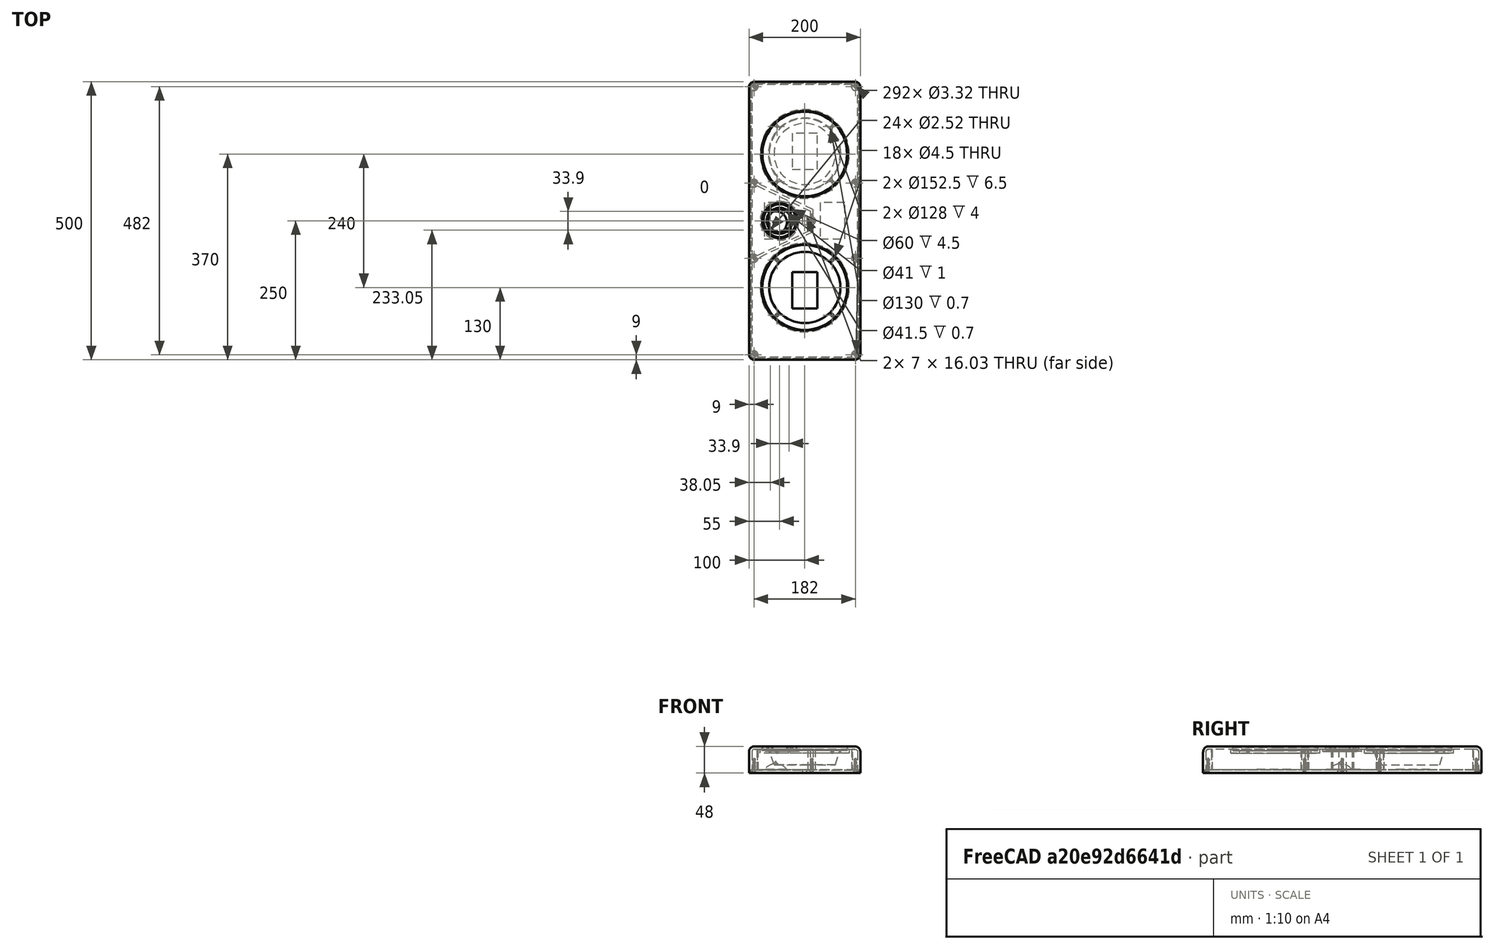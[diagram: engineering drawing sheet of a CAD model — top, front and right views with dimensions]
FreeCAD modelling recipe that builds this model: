
FCSTD DOCUMENT  (FreeCAD 1.1R14555 (Git shallow))
Label: wallspeakers prototype v4
License: All rights reserved
LicenseURL: http://en.wikipedia.org/wiki/All_rights_reserved
objects: Sketcher::SketchObject×23, PartDesign::Pad×11, App::Point×9, PartDesign::Body×9, PartDesign::Pocket×7, TechDraw::DrawViewAnnotation×6, TechDraw::DrawViewImage×6, PartDesign::Hole×5, TechDraw::DrawSVGTemplate×5, TechDraw::DrawPage×5, App::DocumentObjectGroup×4, TechDraw::DrawViewDimExtent×3, PartDesign::Chamfer×3, PartDesign::Revolution×2, PartDesign::Fillet×2, TechDraw::DrawProjGroupItem×2, Spreadsheet::Sheet×1, PartDesign::Thickness×1, TechDraw::DrawProjGroup×1, PartDesign::SubShapeBinder×1, +3 more types
note: 152 computed .brp shape members not serialized (recipe doc carries the construction recipe); baked Part::Feature solids carry a one-line shape summary decoded from their .brp

FEATURE [Spreadsheet::Sheet] Spreadsheet  label="dim"
  cells = A1='ext_width; B1(ext_width)=200; A2='ext_length; B2(ext_length)=500; A3='back_panel_width; B3(back_panel_width)==B1 - B13 * 2; C3='ext_width - rim_width * 2; A4='back_panel_length; B4(back_panel_length)==B2 - B13 * 2; C4='ext_length - rim_width * 2; A5='back_panel_radius; B5(back_panel_radius)==B11 - B13; C5='corner_roundover - rim_width; A6='back_thickness; B6(back_thickness)=5; A7='front_thickness; B7(front_thickness)=5; A8='total_depth; B8(total_depth)=48; C8='giving ourselves 2mm for wall mount fittings etc; A9='wall_thickness; B9(wall_thickness)=5; A10='front_roundover; B10(front_roundover)=10; A11='corner_roundover; B11(corner_roundover)=10; A13='rim_width; B13(rim_width)=3; A14='rim_depth; B14(rim_depth)=5.7; C14='allowing 0.7mm for a compressed 0.8mm gasket; A15='post_diameter; B15(post_diameter)=14; A17='bmr_x; B17(bmr_x)=45; C17='nudging a bit closer to the centre; A18='bmr_y; B18(bmr_y)=0; A19='bmr_screw_distance; B19(bmr_screw_distance)=24; A20='bmr_screw_offset; B20(bmr_screw_offset)=16.95; C20='bmr_screw_distance * sin(45); A21='bmr_hole_diameter; B21(bmr_hole_diameter)=41; A22='bmr_rebate_depth; B22(bmr_rebate_depth)=6; A23='bmr_post_width; B23(bmr_post_width)=7; A24='bmr_rebate_diameter; B24(bmr_rebate_diameter)=60; A26='woofer_x; B26(woofer_x)=0; A27='woofer_y; B27(woofer_y)=120; A28='woofer_support_thickness; B28(woofer_support_thickness)=7; C28='resulting in wall (5mm) + this (7mm) - rebate (8mm) = 5mm; A29='woofer_support_diameter; B29(woofer_support_diameter)=160; A30='woofer_screw_distance; B30(woofer_screw_thickness)=70.05; A31='woofer_screw_offset; B31(woofer_screw_offset)==B30 * 0.707; C31='woofer_screw_distance * sin(45); A32='woofer_hole_diameter; B32(woofer_hole_diameter)=128; A33='woofer_rebate_depth; B33(woofer_rebate_depth)=8; C33='5.3 for woofer rim, 0.7 for compressed gasket, 2 for cone resting excursion; A34='woofer_rebate_diameter; B34(woofer_rebate_diameter)=152.5; A39='woofer cutout spec; B39=127.5; C39=0.3; A40='woofer rebate spec; B40=152; C40=0.3; A41='woofer rebate depth spec; B41=5.3; C41=0.3; A43='gasket thickness (compressed); B43=0.7
FEATURE [Sketcher::SketchObject] Sketch  label="outline"
  ArcFitTolerance = 1e-06
  AttachmentSupport = -> [XY_Plane]
  ExternalTypes = [0]
  FullyConstrained = true
  MakeInternals = false
  MapMode = 5
  expr: Constraints[8] = <<dim>>.ext_width
  expr: Constraints[9] = <<dim>>.ext_length
  sketch-geometry (4):
    g0: LineSegment StartX=-100 StartY=250 StartZ=0 EndX=-100 EndY=-250 EndZ=0
    g1: LineSegment StartX=-100 StartY=-250 StartZ=0 EndX=100 EndY=-250 EndZ=0
    g2: LineSegment StartX=100 StartY=-250 StartZ=0 EndX=100 EndY=250 EndZ=0
    g3: LineSegment StartX=100 StartY=250 StartZ=0 EndX=-100 EndY=250 EndZ=0
  constraints (10):
    c: Coincident(g0,g1)
    c: Coincident(g1,g2)
    c: Coincident(g2,g3)
    c: Coincident(g3,g0)
    c: Vertical(g0)
    c: Horizontal(g1)
    c: Symmetric(g0,g2,g-2)
    c: Symmetric(g2,g1,g-1)
    c: DistanceX(g3,g3) = 200
    c: DistanceY(g2,g2) = 500
FEATURE [PartDesign::Pad] Pad  label="main solid body"
  Direction = (0,0,1)
  Length = 48
  Length2 = 10
  Profile = -> Sketch
  ReferenceAxis = -> Sketch [N_Axis]
  SideType = 0
  Suppressed = false
  Type = 0
  Type2 = 0
  expr: Length = <<dim>>.total_depth
FEATURE [Sketcher::SketchObject] Sketch002  label="woofer rebates"
  ArcFitTolerance = 1e-06
  AttachmentSupport = -> [Pad]
  ExternalTypes = [0]
  FullyConstrained = true
  MakeInternals = false
  MapMode = 5
  Placement = pos=(0,0,48) rot=(0,0,1;0rad)
  expr: Constraints[0] = <<dim>>.woofer_x
  expr: Constraints[1] = <<dim>>.woofer_y
  expr: Constraints[2] = <<dim>>.woofer_rebate_diameter
  expr: Constraints[3] = <<dim>>.woofer_rebate_diameter
  expr: Constraints[4] = <<dim>>.woofer_x
  expr: Constraints[5] = <<dim>>.woofer_y
  sketch-geometry (2):
    g0: Circle CenterX=0 CenterY=120 CenterZ=0 NormalX=0 NormalY=0 NormalZ=1 AngleXU=0 Radius=76.25
    g1: Circle CenterX=0 CenterY=-120 CenterZ=0 NormalX=0 NormalY=0 NormalZ=1 AngleXU=0 Radius=76.25
  constraints (6):
    c: DistanceX(g0,g-1) = 0
    c: DistanceY(g-1,g0) = 120
    c: Diameter(g0) = 152.5
    c: Diameter(g1) = 152.5
    c: DistanceX(g1,g-1) = 0
    c: DistanceY(g1,g-1) = 120
FEATURE [Sketcher::SketchObject] Sketch004  label="bmr rebate"
  ArcFitTolerance = 1e-06
  AttachmentSupport = -> [Pad]
  ExternalTypes = [0]
  FullyConstrained = true
  MakeInternals = false
  MapMode = 5
  Placement = pos=(0,0,48) rot=(0,0,1;0rad)
  expr: Constraints[0] = <<dim>>.bmr_rebate_diameter
  expr: Constraints[2] = <<dim>>.bmr_x
  sketch-geometry (1):
    g0: Circle CenterX=-45 CenterY=0 CenterZ=0 NormalX=0 NormalY=0 NormalZ=1 AngleXU=0 Radius=30
  constraints (3):
    c: Diameter(g0) = 60
    c: PointOnObject(g0,g-1)
    c: DistanceX(g0,g-1) = 45
FEATURE [App::Point] Origin001
  Role = Origin
FEATURE [Sketcher::SketchObject] Sketch010  label="back panel outline"
  ArcFitTolerance = 1e-06
  AttachmentSupport = -> [XY_Plane002]
  ExternalTypes = [0]
  FullyConstrained = true
  MakeInternals = false
  MapMode = 5
  expr: Constraints[17] = <<dim>>.back_panel_radius
  expr: Constraints[18] = <<dim>>.back_panel_width
  expr: Constraints[19] = <<dim>>.back_panel_length
  sketch-geometry (10):
    g0: LineSegment StartX=-97 StartY=240 StartZ=0 EndX=-97 EndY=-240 EndZ=0
    g1: LineSegment StartX=-90 StartY=-247 StartZ=0 EndX=90 EndY=-247 EndZ=0
    g2: LineSegment StartX=97 StartY=-240 StartZ=0 EndX=97 EndY=240 EndZ=0
    g3: LineSegment StartX=90 StartY=247 StartZ=0 EndX=-90 EndY=247 EndZ=0
    g4: ArcOfCircle CenterX=-90 CenterY=240 CenterZ=0 NormalX=0 NormalY=0 NormalZ=1 AngleXU=0 Radius=7 StartAngle=1.5708 EndAngle=3.14159
    g5: ArcOfCircle CenterX=-90 CenterY=-240 CenterZ=0 NormalX=0 NormalY=0 NormalZ=1 AngleXU=0 Radius=7 StartAngle=3.14159 EndAngle=4.71239
    g6: ArcOfCircle CenterX=90 CenterY=-240 CenterZ=0 NormalX=0 NormalY=0 NormalZ=1 AngleXU=0 Radius=7 StartAngle=4.71239 EndAngle=6.28319
    g7: ArcOfCircle CenterX=90 CenterY=240 CenterZ=0 NormalX=0 NormalY=0 NormalZ=1 AngleXU=0 Radius=7 StartAngle=1.3e-15 EndAngle=1.5708
    g8: GeomPoint [constr] X=-97 Y=247 Z=0
    g9: GeomPoint [constr] X=97 Y=-247 Z=0
  constraints (22):
    c: Tangent(g0,g4) = -1.5708
    c: Tangent(g0,g5) = -1.5708
    c: Tangent(g1,g5) = -1.5708
    c: Tangent(g1,g6) = -1.5708
    c: Tangent(g2,g6) = -1.5708
    c: Tangent(g2,g7) = -1.5708
    c: Tangent(g3,g7) = -1.5708
    c: Tangent(g3,g4) = -1.5708
    c: Vertical(g0)
    c: Vertical(g2)
    c: Horizontal(g1)
    c: Horizontal(g3)
    c: Equal(g5,g6)
    c: PointOnObject(g8,g0)
    c: PointOnObject(g8,g3)
    c: PointOnObject(g9,g1)
    c: PointOnObject(g9,g2)
    c: Radius(g5) = 7
    c: DistanceX(g0,g2) = 194
    c: DistanceY(g1,g3) = 494
    c: Symmetric(g0,g2,g-2)
    c: Symmetric(g3,g1,g-1)
FEATURE [PartDesign::Pad] Pad004  label="back panel pad"
  Direction = (0,0,1)
  Length = 5
  Length2 = 10
  Profile = -> Sketch010
  ReferenceAxis = -> Sketch010 [N_Axis]
  SideType = 0
  Suppressed = false
  Type = 0
  Type2 = 0
  expr: Length = <<dim>>.back_thickness
FEATURE [App::Point] Origin005
  Role = Origin
FEATURE [App::Point] Origin007
  Role = Origin
FEATURE [App::Point] Origin009
  Role = Origin
FEATURE [Sketcher::SketchObject] Sketch017  label="Woofer gasket"
  ArcFitTolerance = 1e-06
  AttachmentSupport = -> [Origin008]
  ExternalTypes = [0]
  FullyConstrained = true
  MakeInternals = false
  MapMode = 5
  expr: Constraints[0] = <<dim>>.woofer_rebate_diameter - 0.5
  expr: Constraints[11] = <<dim>>.woofer_screw_offset
  expr: Constraints[12] = <<dim>>.woofer_screw_offset
  expr: Constraints[1] = <<dim>>.woofer_hole_diameter + 2
  sketch-geometry (6):
    g0: Circle CenterX=0 CenterY=0 CenterZ=0 NormalX=0 NormalY=0 NormalZ=1 AngleXU=0 Radius=76
    g1: Circle CenterX=0 CenterY=0 CenterZ=0 NormalX=0 NormalY=0 NormalZ=1 AngleXU=0 Radius=65
    g2: Circle CenterX=49.5253 CenterY=-49.5253 CenterZ=0 NormalX=0 NormalY=0 NormalZ=1 AngleXU=0 Radius=2.125
    g3: Circle CenterX=49.5253 CenterY=49.5253 CenterZ=0 NormalX=0 NormalY=0 NormalZ=1 AngleXU=0 Radius=2.125
    g4: Circle CenterX=-49.5253 CenterY=49.5253 CenterZ=0 NormalX=0 NormalY=0 NormalZ=1 AngleXU=0 Radius=2.125
    g5: Circle CenterX=-49.5253 CenterY=-49.5253 CenterZ=0 NormalX=0 NormalY=0 NormalZ=1 AngleXU=0 Radius=2.125
  constraints (13):
    c: Diameter(g0) = 152
    c: Diameter(g1) = 130
    c: Coincident(g0,g1)
    c: Coincident(g-1,g0)
    c: Equal(g2,g3)
    c: Equal(g2,g4)
    c: Equal(g2,g5)
    c: Diameter(g2) = 4.25
    c: Symmetric(g4,g3,g-2)
    c: Symmetric(g5,g2,g-2)
    c: Symmetric(g4,g5,g-1)
    c: DistanceX(g-1,g3) = 49.5253
    c: DistanceY(g-1,g3) = 49.5253
FEATURE [Sketcher::SketchObject] Sketch018  label="screw posts sketch"
  ArcFitTolerance = 1e-06
  AttachmentOffset = pos=(0,0,-5.7) rot=(0,0,1;0rad)
  AttachmentSupport = -> [Pad]
  ExternalTypes = [0]
  FullyConstrained = true
  MakeInternals = false
  MapMode = 5
  Placement = pos=(0,0,5.7) rot=(1,0,0;3.14159rad)
  expr: .AttachmentOffset.Base.z = -<<dim>>.rim_depth
  expr: Constraints[0] = <<dim>>.ext_length / 2 - <<dim>>.post_diameter / 2 - 2
  expr: Constraints[1] = <<dim>>.ext_width / 2 - <<dim>>.post_diameter / 2 - 2
  expr: Constraints[20] = <<dim>>.post_diameter
  expr: Constraints[4] = <<dim>>.ext_width / 2 - <<dim>>.post_diameter / 2 - 2
  sketch-geometry (9):
    g0: Circle CenterX=-91 CenterY=241 CenterZ=0 NormalX=0 NormalY=0 NormalZ=1 AngleXU=0 Radius=7
    g1: Circle CenterX=91 CenterY=241 CenterZ=0 NormalX=0 NormalY=0 NormalZ=1 AngleXU=0 Radius=7
    g2: Circle CenterX=-91 CenterY=67.5 CenterZ=0 NormalX=0 NormalY=0 NormalZ=1 AngleXU=0 Radius=7
    g3: Circle CenterX=12.5 CenterY=0 CenterZ=0 NormalX=0 NormalY=0 NormalZ=1 AngleXU=0 Radius=7
    g4: Circle CenterX=-91 CenterY=-67.5 CenterZ=0 NormalX=0 NormalY=0 NormalZ=1 AngleXU=0 Radius=7
    g5: Circle CenterX=91 CenterY=67.5 CenterZ=0 NormalX=0 NormalY=0 NormalZ=1 AngleXU=0 Radius=7
    g6: Circle CenterX=91 CenterY=-67.5 CenterZ=0 NormalX=0 NormalY=0 NormalZ=1 AngleXU=0 Radius=7
    g7: Circle CenterX=-91 CenterY=-241 CenterZ=0 NormalX=0 NormalY=0 NormalZ=1 AngleXU=0 Radius=7
    g8: Circle CenterX=91 CenterY=-241 CenterZ=0 NormalX=0 NormalY=0 NormalZ=1 AngleXU=0 Radius=7
  constraints (14):
    c: DistanceY(g-1,g0) = 241
    c: DistanceX(g0,g-1) = 91
    c: Symmetric(g0,g1,g-2)
    c: DistanceY(g-1,g2) = 67.5
    c: DistanceX(g2,g-1) = 91
    c: DistanceX(g-1,g3) = 12.5
    c: PointOnObject(g3,g-1)
    c: Symmetric(g2,g4,g-1)
    c: Symmetric(g2,g5,g-2)
    c: Symmetric(g5,g6,g-1)
    c: Symmetric(g1,g8,g-1)
    c: Symmetric(g0,g7,g-1)
    c: Equal(g0, g1-g8) x8
    c: Diameter(g0) = 14
FEATURE [App::Point] Origin011
  Role = Origin
FEATURE [Sketcher::SketchObject] Sketch019
  ArcFitTolerance = 1e-06
  AttachmentSupport = -> [Origin010]
  ExternalTypes = [0]
  FullyConstrained = true
  MakeInternals = false
  MapMode = 5
  Placement = pos=(0,0,0) rot=(0.57735,0.57735,0.57735;2.0944rad)
  sketch-geometry (6):
    g0: LineSegment StartX=0 StartY=32 StartZ=0 EndX=-76 EndY=32 EndZ=0
    g1: LineSegment StartX=-76 StartY=32 StartZ=0 EndX=-76 EndY=26.7 EndZ=0
    g2: LineSegment StartX=-76 StartY=26.7 StartZ=0 EndX=-63.75 EndY=26.7 EndZ=0
    g3: LineSegment StartX=-63.75 StartY=26.7 StartZ=0 EndX=-55 EndY=6e-16 EndZ=0
    g4: LineSegment StartX=-55 StartY=6e-16 StartZ=0 EndX=0 EndY=6e-16 EndZ=0
    g5: LineSegment StartX=0 StartY=6e-16 StartZ=0 EndX=0 EndY=32 EndZ=0
  constraints (17):
    c: PointOnObject(g0,g-2)
    c: Horizontal(g0)
    c: Coincident(g0,g1)
    c: Vertical(g1)
    c: Coincident(g1,g2)
    c: Horizontal(g2)
    c: Coincident(g2,g3)
    c: Coincident(g3,g4)
    c: Horizontal(g4)
    c: Coincident(g4,g5)
    c: Coincident(g5,g0)
    c: DistanceX(g0,g0) = 76
    c: DistanceY(g1,g1) = 5.3
    c: DistanceX(g2,g-1) = 63.75
    c: DistanceX(g3,g-1) = 55
    c: DistanceY(g5,g5) = 32
    c: Coincident(g4,g-1)
FEATURE [PartDesign::Revolution] Revolution
  Angle = 360
  Angle2 = 60
  Axis = (0,0,1)
  Base = (0,0,0)
  Profile = -> Sketch019
  ReferenceAxis = -> Sketch019 [V_Axis]
  Suppressed = false
  Type = 0
FEATURE [PartDesign::Body] Body005  label="woofer rough model for fitting"
  AllowCompound = false
  Group = -> [Sketch019,Revolution]
  Origin = -> Origin010
  Placement = pos=(0,120,15) rot=(0,0,1;0rad)
  Tip = -> Revolution
FEATURE [PartDesign::Pad] Pad010  label="woofer gasket pad"
  Direction = (0,0,1)
  Length = 0.7
  Length2 = 10
  Profile = -> Sketch017
  ReferenceAxis = -> Sketch017 [N_Axis]
  SideType = 0
  Suppressed = false
  Type = 0
  Type2 = 0
FEATURE [PartDesign::Body] Body004  label="woofer gasket"
  AllowCompound = false
  Group = -> [Sketch017,Pad010]
  Origin = -> Origin008
  Placement = pos=(0,120,40) rot=(0,0,1;0rad)
  Tip = -> Pad010
  expr: .Placement.Base.y = <<dim>>.woofer_y
  expr: .Placement.Base.z = <<dim>>.total_depth - <<dim>>.woofer_rebate_depth
FEATURE [App::Point] Origin015
  Role = Origin
FEATURE [Sketcher::SketchObject] Sketch020
  ArcFitTolerance = 1e-06
  AttachmentSupport = -> [Origin014]
  ExternalTypes = [0]
  FullyConstrained = true
  MakeInternals = false
  MapMode = 5
  sketch-geometry (6):
    g0: Circle CenterX=0 CenterY=0 CenterZ=0 NormalX=0 NormalY=0 NormalZ=1 AngleXU=0 Radius=30
    g1: Circle CenterX=0 CenterY=0 CenterZ=0 NormalX=0 NormalY=0 NormalZ=1 AngleXU=0 Radius=20.75
    g2: Circle CenterX=16.95 CenterY=-16.95 CenterZ=0 NormalX=0 NormalY=0 NormalZ=1 AngleXU=0 Radius=1.75
    g3: Circle CenterX=16.95 CenterY=16.95 CenterZ=0 NormalX=0 NormalY=0 NormalZ=1 AngleXU=0 Radius=1.75
    g4: Circle CenterX=-16.95 CenterY=16.95 CenterZ=0 NormalX=0 NormalY=0 NormalZ=1 AngleXU=0 Radius=1.75
    g5: Circle CenterX=-16.95 CenterY=-16.95 CenterZ=0 NormalX=0 NormalY=0 NormalZ=1 AngleXU=0 Radius=1.75
  constraints (13):
    c: Diameter(g0) = 60
    c: Diameter(g1) = 41.5
    c: Coincident(g0,g1)
    c: Coincident(g-1,g0)
    c: Equal(g2,g3)
    c: Equal(g2,g4)
    c: Equal(g2,g5)
    c: Diameter(g2) = 3.5
    c: Symmetric(g4,g3,g-2)
    c: Symmetric(g5,g2,g-2)
    c: Symmetric(g4,g5,g-1)
    c: DistanceX(g-1,g3) = 16.95
    c: DistanceY(g-1,g3) = 16.95
FEATURE [PartDesign::Pad] Pad011
  Direction = (0,0,1)
  Length = 0.7
  Length2 = 10
  Profile = -> Sketch020
  ReferenceAxis = -> Sketch020 [N_Axis]
  SideType = 0
  Suppressed = false
  Type = 0
  Type2 = 0
FEATURE [PartDesign::Body] Body007  label="bmr gasket"
  AllowCompound = false
  Group = -> [Sketch020,Pad011]
  Origin = -> Origin014
  Placement = pos=(-45,0,42) rot=(0,0,1;0rad)
  Tip = -> Pad011
  expr: .Placement.Base.x = -<<dim>>.bmr_x
  expr: .Placement.Base.z = <<dim>>.total_depth - <<dim>>.bmr_rebate_depth
FEATURE [Sketcher::SketchObject] Sketch021  label="rim sketch"
  ArcFitTolerance = 1e-06
  AttachmentSupport = -> [Pad]
  ExternalTypes = [0]
  FullyConstrained = true
  MakeInternals = false
  MapMode = 5
  Placement = pos=(0,0,0) rot=(1,0,0;3.14159rad)
  expr: Constraints[18] = <<dim>>.ext_width - <<dim>>.rim_width * 2
  expr: Constraints[19] = <<dim>>.ext_length - <<dim>>.rim_width * 2
  sketch-geometry (10):
    g0: LineSegment StartX=-97 StartY=239.5 StartZ=0 EndX=-97 EndY=-239.5 EndZ=0
    g1: LineSegment StartX=-89.5 StartY=-247 StartZ=0 EndX=89.5 EndY=-247 EndZ=0
    g2: LineSegment StartX=97 StartY=-239.5 StartZ=0 EndX=97 EndY=239.5 EndZ=0
    g3: LineSegment StartX=89.5 StartY=247 StartZ=0 EndX=-89.5 EndY=247 EndZ=0
    g4: ArcOfCircle CenterX=-89.5 CenterY=239.5 CenterZ=0 NormalX=0 NormalY=0 NormalZ=1 AngleXU=0 Radius=7.5 StartAngle=1.5708 EndAngle=3.14159
    g5: ArcOfCircle CenterX=-89.5 CenterY=-239.5 CenterZ=0 NormalX=0 NormalY=0 NormalZ=1 AngleXU=0 Radius=7.5 StartAngle=3.14159 EndAngle=4.71239
    g6: ArcOfCircle CenterX=89.5 CenterY=-239.5 CenterZ=0 NormalX=0 NormalY=0 NormalZ=1 AngleXU=0 Radius=7.5 StartAngle=4.71239 EndAngle=6.28319
    g7: ArcOfCircle CenterX=89.5 CenterY=239.5 CenterZ=0 NormalX=0 NormalY=0 NormalZ=1 AngleXU=0 Radius=7.5 StartAngle=0 EndAngle=1.5708
    g8: GeomPoint [constr] X=-97 Y=247 Z=0
    g9: GeomPoint [constr] X=97 Y=-247 Z=0
  constraints (22):
    c: Tangent(g0,g4) = -1.5708
    c: Tangent(g0,g5) = -1.5708
    c: Tangent(g1,g5) = -1.5708
    c: Tangent(g1,g6) = -1.5708
    c: Tangent(g2,g6) = -1.5708
    c: Tangent(g2,g7) = -1.5708
    c: Tangent(g3,g7) = -1.5708
    c: Tangent(g3,g4) = -1.5708
    c: Vertical(g0)
    c: Vertical(g2)
    c: Horizontal(g1)
    c: Horizontal(g3)
    c: Equal(g5,g6)
    c: PointOnObject(g8,g0)
    c: PointOnObject(g8,g3)
    c: PointOnObject(g9,g1)
    c: PointOnObject(g9,g2)
    c: Radius(g5) = 7.5
    c: DistanceX(g0,g2) = 194
    c: DistanceY(g1,g3) = 494
    c: Symmetric(g0,g2,g-2)
    c: Symmetric(g3,g1,g-1)
FEATURE [Sketcher::SketchObject] Sketch024  label="cable entry hole sketch"
  ArcFitTolerance = 1e-06
  ExternalTypes = [0]
  FullyConstrained = true
  MakeInternals = false
  MapMode = 5
  Placement = pos=(0,0,0) rot=(1,0,0;3.14159rad)
  sketch-geometry (4):
    g0: LineSegment StartX=-3.5 StartY=8.015 StartZ=0 EndX=-3.5 EndY=-8.015 EndZ=0
    g1: LineSegment StartX=-3.5 StartY=-8.015 StartZ=0 EndX=3.5 EndY=-8.015 EndZ=0
    g2: LineSegment StartX=3.5 StartY=-8.015 StartZ=0 EndX=3.5 EndY=8.015 EndZ=0
    g3: LineSegment StartX=3.5 StartY=8.015 StartZ=0 EndX=-3.5 EndY=8.015 EndZ=0
  constraints (10):
    c: Coincident(g0,g1)
    c: Coincident(g1,g2)
    c: Coincident(g2,g3)
    c: Coincident(g3,g0)
    c: Vertical(g0)
    c: Horizontal(g1)
    c: DistanceY(g0,g0) = 16.03
    c: DistanceX(g3,g3) = 7
    c: Symmetric(g0,g2,g-2)
    c: Symmetric(g2,g1,g-1)
FEATURE [PartDesign::Pocket] Pocket004  label="cable entry hole"
  BaseFeature = -> Pad004
  Direction = (0,1e-16,1)
  Length = 5
  Length2 = 5
  Profile = -> Sketch024
  ReferenceAxis = -> Sketch024 [N_Axis]
  SideType = 0
  Suppressed = false
  Type = 0
  Type2 = 0
FEATURE [Sketcher::SketchObject] Sketch027
  ArcFitTolerance = 1e-06
  AttachmentSupport = -> [Origin006]
  ExternalTypes = [0]
  FullyConstrained = true
  MakeInternals = false
  MapMode = 5
  sketch-geometry (4):
    g0: ArcOfCircle CenterX=0 CenterY=0 CenterZ=0 NormalX=0 NormalY=0 NormalZ=1 AngleXU=0 Radius=29.9 StartAngle=1.5708 EndAngle=3.14159
    g1: LineSegment StartX=1.3e-15 StartY=29.9 StartZ=0 EndX=1.3e-15 EndY=20.5 EndZ=0
    g2: LineSegment StartX=-29.9 StartY=2.5e-15 StartZ=0 EndX=-20.5 EndY=2.5e-15 EndZ=0
    g3: ArcOfCircle CenterX=0 CenterY=0 CenterZ=0 NormalX=0 NormalY=0 NormalZ=1 AngleXU=0 Radius=20.5 StartAngle=1.5708 EndAngle=3.14159
  constraints (13):
    c: Coincident(g0,g-1)
    c: PointOnObject(g3,g-1)
    c: PointOnObject(g3,g-2)
    c: Vertical(g1)
    c: PointOnObject(g1,g-2)
    c: Horizontal(g2)
    c: PointOnObject(g2,g-1)
    c: Diameter(g0) = 59.8
    c: Coincident(g1,g0)
    c: Coincident(g2,g0)
    c: Coincident(g1,g3)
    c: Radius(g3) = 20.5
    c: Coincident(g3,g2)
FEATURE [PartDesign::Pad] Pad013  label="base pad"
  Direction = (0,0,1)
  Length = 5
  Length2 = 10
  Profile = -> Sketch027
  ReferenceAxis = -> Sketch027 [N_Axis]
  SideType = 0
  Suppressed = false
  Type = 0
  Type2 = 0
FEATURE [Sketcher::SketchObject] Sketch015  label="frame outline"
  ArcFitTolerance = 1e-06
  AttachmentSupport = -> [Pad013]
  ExternalTypes = [0]
  FullyConstrained = true
  MakeInternals = false
  MapMode = 5
  Placement = pos=(0,0,5) rot=(0,0,1;0rad)
  sketch-geometry (8):
    g0: ArcOfCircle CenterX=0 CenterY=0 CenterZ=0 NormalX=0 NormalY=0 NormalZ=1 AngleXU=0 Radius=20.5 StartAngle=1.5708 EndAngle=3.14159
    g1: ArcOfCircle CenterX=0 CenterY=0 CenterZ=0 NormalX=0 NormalY=0 NormalZ=1 AngleXU=0 Radius=23.25 StartAngle=2.58919 EndAngle=3.14159
    g2: ArcOfCircle CenterX=-16.8247 CenterY=16.8336 CenterZ=0 NormalX=0 NormalY=0 NormalZ=1 AngleXU=0 Radius=3.72 StartAngle=0.960084 EndAngle=3.75505
    g3: ArcOfCircle CenterX=-21.785 CenterY=13.3876 CenterZ=0 NormalX=0 NormalY=0 NormalZ=1 AngleXU=0 Radius=2.32 StartAngle=5.74581 EndAngle=6.88028
    g4: ArcOfCircle CenterX=-13.3758 CenterY=21.792 CenterZ=0 NormalX=0 NormalY=0 NormalZ=1 AngleXU=0 Radius=2.32 StartAngle=4.10939 EndAngle=5.24385
    g5: LineSegment StartX=1.4e-15 StartY=20.5 StartZ=0 EndX=1.4e-15 EndY=23.25 EndZ=0
    g6: LineSegment StartX=-20.5 StartY=2.5e-15 StartZ=0 EndX=-23.25 EndY=2.5e-15 EndZ=0
    g7: ArcOfCircle CenterX=0 CenterY=0 CenterZ=0 NormalX=0 NormalY=0 NormalZ=1 AngleXU=0 Radius=23.25 StartAngle=1.5708 EndAngle=2.1232
  constraints (28):
    c: Coincident(g0,g-1)
    c: PointOnObject(g1,g-1)
    c: PointOnObject(g1,g-2)
    c: DistanceX(g7,g-1) = 12.2
    c: DistanceY(g-1,g1) = 12.2
    c: Radius(g2) = 3.72
    c: Coincident(g3,g2)
    c: Coincident(g3,g1)
    c: Coincident(g4,g7)
    c: Coincident(g4,g2)
    c: Radius(g3) = 2.32
    c: Radius(g4) = 2.32
    c: Angle(g3) = 1.13446
    c: Angle(g4) = 1.13446
    c: Distance(g2,g-1) = 23.8
    c: Angle(g2) = 2.79497
    c: Vertical(g5)
    c: PointOnObject(g5,g-2)
    c: Horizontal(g6)
    c: PointOnObject(g6,g-1)
    c: Diameter(g0) = 41
    c: Coincident(g5,g0)
    c: Coincident(g6,g0)
    c: Diameter(g1) = 46.5
    c: Coincident(g5,g7)
    c: Coincident(g6,g1)
    c: Coincident(g1,g7)
    c: Radius(g7) = 23.25
FEATURE [App::Point] Origin019
  Role = Origin
FEATURE [Sketcher::SketchObject] Sketch030
  ArcFitTolerance = 1e-06
  AttachmentOffset = pos=(-52,6.35,3) rot=(0,0,1;0rad)
  AttachmentSupport = -> [Origin018]
  ExternalTypes = [0]
  FullyConstrained = true
  MakeInternals = false
  MapMode = 5
  Placement = pos=(-52,-3,6.35) rot=(1,0,0;1.5708rad)
  sketch-geometry (10):
    g0: LineSegment StartX=0 StartY=0 StartZ=0 EndX=20 EndY=-3.2e-14 EndZ=0
    g1: LineSegment StartX=0 StartY=0 StartZ=0 EndX=0 EndY=15 EndZ=0
    g2: ArcOfCircle CenterX=0 CenterY=-14.2 CenterZ=0 NormalX=0 NormalY=0 NormalZ=1 AngleXU=0 Radius=24.5284 StartAngle=0.617406 EndAngle=1.40699
    g3-g6: Circle [constr] x4 (B-spline internal-alignment scaffolding for g7; pole/knot coordinates omitted)
    g7: BSplineCurve PolesCount=4 KnotsCount=2 Degree=3 IsPeriodic=0
    g8: GeomPoint [constr] X=4 Y=10 Z=0
    g9: GeomPoint [constr] X=0 Y=15 Z=0
  constraints (23):
    c: Coincident(g0,g-1)
    c: PointOnObject(g0,g-1)
    c: Coincident(g1,g0)
    c: PointOnObject(g1,g-2)
    c: DistanceY(g1,g1) = 15
    c: DistanceX(g0,g0) = 20
    c: Coincident(g2,g0)
    c: PointOnObject(g2,g-2)
    c: Distance(g2,g-2) = 4
    c: DistanceY(g-1,g2) = 10
    c: Weight(g3) = 1
    c: Equal(g3,g4)
    c: Equal(g3,g5)
    c: Equal(g3,g6)
    c: InternalAlignment(g3-g6 -> g7) x4
    c: InternalAlignment(g8,g7)
    c: InternalAlignment(g9,g7)
    c: Coincident(g3,g2)
    c: Coincident(g6,g1)
    c: DistanceY(g-1,g5) = 14
    c: DistanceX(g-1,g5) = 0.85
    c: DistanceY(g-1,g4) = 10.9
    c: DistanceX(g-1,g4) = 1.5
FEATURE [PartDesign::Revolution] Revolution001
  Angle = 360
  Angle2 = 60
  Axis = (0,2e-16,1)
  Base = (-52,-3,6.35)
  Profile = -> Sketch030
  ReferenceAxis = -> Sketch030 [V_Axis]
  Reversed = true
  Suppressed = false
  Type = 0
FEATURE [PartDesign::Body] Body008  label="BMR backwave diffuser"
  AllowCompound = false
  Group = -> [Sketch030,Revolution001]
  Origin = -> Origin018
  Tip = -> Revolution001
FEATURE [App::DocumentObjectGroup] Group004  label="External models for fitting"
  Group = -> [Body005]
FEATURE [PartDesign::Thickness] Thickness001  label="thickness main body"
  Base = -> Pad [Face5]
  BaseFeature = -> Pad
  Intersection = false
  Join = 0
  Mode = 0
  Reversed = true
  SupportTransform = false
  Suppressed = false
  Value = 5
FEATURE [Sketcher::SketchObject] Sketch001  label="driver holes"
  ArcFitTolerance = 1e-06
  AttachmentSupport = -> [Thickness001]
  ExternalTypes = [0]
  FullyConstrained = true
  MakeInternals = false
  MapMode = 5
  Placement = pos=(0,0,48) rot=(0,0,1;0rad)
  expr: Constraints[0] = <<dim>>.bmr_hole_diameter
  expr: Constraints[2] = <<dim>>.bmr_x
  expr: Constraints[3] = <<dim>>.woofer_x
  expr: Constraints[4] = <<dim>>.woofer_y
  expr: Constraints[5] = <<dim>>.woofer_hole_diameter
  expr: Constraints[6] = <<dim>>.woofer_hole_diameter
  expr: Constraints[7] = <<dim>>.woofer_x
  expr: Constraints[8] = <<dim>>.woofer_y
  sketch-geometry (3):
    g0: Circle CenterX=-45 CenterY=0 CenterZ=0 NormalX=0 NormalY=0 NormalZ=1 AngleXU=0 Radius=20.5
    g1: Circle CenterX=0 CenterY=120 CenterZ=0 NormalX=0 NormalY=0 NormalZ=1 AngleXU=0 Radius=64
    g2: Circle CenterX=0 CenterY=-120 CenterZ=0 NormalX=0 NormalY=0 NormalZ=1 AngleXU=0 Radius=64
  constraints (9):
    c: Diameter(g0) = 41
    c: PointOnObject(g0,g-1)
    c: DistanceX(g0,g-1) = 45
    c: DistanceX(g1,g-1) = 0
    c: DistanceY(g-1,g1) = 120
    c: Diameter(g1) = 128
    c: Diameter(g2) = 128
    c: DistanceX(g2,g-1) = 0
    c: DistanceY(g2,g-1) = 120
FEATURE [Sketcher::SketchObject] Sketch003  label="woofer support rings"
  ArcFitTolerance = 1e-06
  AttachmentSupport = -> [Thickness001]
  ExternalTypes = [0]
  FullyConstrained = true
  MakeInternals = false
  MapMode = 5
  Placement = pos=(0,0,43) rot=(1,0,0;3.14159rad)
  expr: Constraints[0] = <<dim>>.woofer_x
  expr: Constraints[11] = <<dim>>.woofer_y
  expr: Constraints[1] = <<dim>>.woofer_y
  expr: Constraints[2] = <<dim>>.woofer_hole_diameter
  expr: Constraints[3] = <<dim>>.woofer_hole_diameter
  expr: Constraints[4] = <<dim>>.woofer_x
  expr: Constraints[5] = <<dim>>.woofer_y
  expr: Constraints[7] = <<dim>>.woofer_y
  expr: Constraints[8] = <<dim>>.woofer_support_diameter
  expr: Constraints[9] = <<dim>>.woofer_support_diameter
  sketch-geometry (4):
    g0: Circle CenterX=0 CenterY=120 CenterZ=0 NormalX=0 NormalY=0 NormalZ=1 AngleXU=0 Radius=64
    g1: Circle CenterX=0 CenterY=-120 CenterZ=0 NormalX=0 NormalY=0 NormalZ=1 AngleXU=0 Radius=64
    g2: Circle CenterX=0 CenterY=120 CenterZ=0 NormalX=0 NormalY=0 NormalZ=1 AngleXU=0 Radius=80
    g3: Circle CenterX=0 CenterY=-120 CenterZ=0 NormalX=0 NormalY=0 NormalZ=1 AngleXU=0 Radius=80
  constraints (12):
    c: DistanceX(g0,g-1) = 0
    c: DistanceY(g-1,g0) = 120
    c: Diameter(g0) = 128
    c: Diameter(g1) = 128
    c: DistanceX(g1,g-1) = 0
    c: DistanceY(g1,g-1) = 120
    c: DistanceX(g2,g-1) = 0
    c: DistanceY(g-1,g2) = 120
    c: Diameter(g2) = 160
    c: Diameter(g3) = 160
    c: DistanceX(g3,g-1) = 0
    c: DistanceY(g3,g-1) = 120
FEATURE [Sketcher::SketchObject] Sketch008  label="bmr support ring"
  ArcFitTolerance = 1e-06
  AttachmentSupport = -> [Thickness001]
  ExternalTypes = [0]
  FullyConstrained = true
  MakeInternals = true
  MapMode = 5
  Placement = pos=(0,0,43) rot=(1,0,0;3.14159rad)
  expr: Constraints[0] = <<dim>>.bmr_rebate_diameter + 10
  expr: Constraints[2] = <<dim>>.bmr_x
  expr: Constraints[3] = <<dim>>.bmr_hole_diameter
  expr: Constraints[5] = <<dim>>.bmr_x
  sketch-geometry (2):
    g0: Circle CenterX=-45 CenterY=0 CenterZ=0 NormalX=0 NormalY=0 NormalZ=1 AngleXU=0 Radius=35
    g1: Circle CenterX=-45 CenterY=0 CenterZ=0 NormalX=0 NormalY=0 NormalZ=1 AngleXU=0 Radius=20.5
  constraints (6):
    c: Diameter(g0) = 70
    c: PointOnObject(g0,g-1)
    c: DistanceX(g0,g-1) = 45
    c: Diameter(g1) = 41
    c: PointOnObject(g1,g-1)
    c: DistanceX(g1,g-1) = 45
FEATURE [Sketcher::SketchObject] Sketch031  label="internal baffle sketch"
  ArcFitTolerance = 1e-06
  AttachmentSupport = -> [Thickness001]
  ExternalTypes = [0]
  FullyConstrained = true
  MakeInternals = false
  MapMode = 5
  Placement = pos=(0,0,43) rot=(1,0,0;3.14159rad)
  sketch-geometry (12):
    g0: LineSegment StartX=15 StartY=20 StartZ=0 EndX=15 EndY=-20 EndZ=0
    g1: LineSegment StartX=15 StartY=-20 StartZ=0 EndX=-90 EndY=-70 EndZ=0
    g2: LineSegment StartX=-90 StartY=-70 StartZ=0 EndX=-95 EndY=-70 EndZ=0
    g3: LineSegment StartX=15 StartY=20 StartZ=0 EndX=-90 EndY=70 EndZ=0
    g4: LineSegment StartX=-90 StartY=70 StartZ=0 EndX=-95 EndY=70 EndZ=0
    g5: LineSegment StartX=-95 StartY=-70 StartZ=0 EndX=-95 EndY=-65 EndZ=0
    g6: LineSegment StartX=-95 StartY=-65 StartZ=0 EndX=-90 EndY=-65 EndZ=0
    g7: LineSegment StartX=-90 StartY=-65 StartZ=0 EndX=10 EndY=-17.381 EndZ=0
    g8: LineSegment StartX=10 StartY=-17.381 StartZ=0 EndX=10 EndY=17.381 EndZ=0
    g9: LineSegment StartX=10 StartY=17.381 StartZ=0 EndX=-90 EndY=65 EndZ=0
    g10: LineSegment StartX=-90 StartY=65 StartZ=0 EndX=-95 EndY=65 EndZ=0
    g11: LineSegment StartX=-95 StartY=65 StartZ=0 EndX=-95 EndY=70 EndZ=0
  constraints (31):
    c: Parallel(g9,g3)
    c: Parallel(g7,g1)
    c: Parallel(g6,g2)
    c: Parallel(g4,g10)
    c: Coincident(g8,g9)
    c: Coincident(g8,g7)
    c: Coincident(g1,g0)
    c: Coincident(g0,g3)
    c: Coincident(g6,g5)
    c: Coincident(g5,g2)
    c: Coincident(g2,g1)
    c: Coincident(g7,g6)
    c: Coincident(g4,g3)
    c: Coincident(g9,g10)
    c: Coincident(g11,g10)
    c: Coincident(g4,g11)
    c: Symmetric(g0,g0,g-1)
    c: Symmetric(g8,g7,g-1)
    c: DistanceY(g11,g11) = 5
    c: Symmetric(g10,g5,g-1)
    c: Symmetric(g4,g2,g-1)
    c: Symmetric(g9,g6,g-1)
    c: Horizontal(g4)
    c: Distance(g9,g3) = 5
    c: DistanceX(g-1,g8) = 10
    c: DistanceX(g4,g4) = 5
    c: DistanceX(g8,g0) = 5
    c: DistanceX(g4,g-1) = 95
    c: DistanceY(g-1,g4) = 70
    c: Vertical(g5)
    c: DistanceY(g-1,g0) = 20
FEATURE [Sketcher::SketchObject] Sketch032  label="cc of screw posts sketch"
  ArcFitTolerance = 1e-06
  AttachmentSupport = -> [Pad004]
  ExternalTypes = [0]
  FullyConstrained = true
  MakeInternals = false
  MapMode = 5
  Placement = pos=(0,0,0) rot=(1,0,0;3.14159rad)
  expr: Constraints[0] = Sketch018.Constraints[0]
  expr: Constraints[1] = Sketch018.Constraints[1]
  expr: Constraints[20] = Sketch018.Constraints[20]
  expr: Constraints[3] = Sketch018.Constraints[3]
  expr: Constraints[4] = Sketch018.Constraints[4]
  expr: Constraints[5] = Sketch018.Constraints[5]
  sketch-geometry (9):
    g0: Circle CenterX=-91 CenterY=241 CenterZ=0 NormalX=0 NormalY=0 NormalZ=1 AngleXU=0 Radius=7
    g1: Circle CenterX=91 CenterY=241 CenterZ=0 NormalX=0 NormalY=0 NormalZ=1 AngleXU=0 Radius=7
    g2: Circle CenterX=-91 CenterY=67.5 CenterZ=0 NormalX=0 NormalY=0 NormalZ=1 AngleXU=0 Radius=7
    g3: Circle CenterX=12.5 CenterY=0 CenterZ=0 NormalX=0 NormalY=0 NormalZ=1 AngleXU=0 Radius=7
    g4: Circle CenterX=-91 CenterY=-67.5 CenterZ=0 NormalX=0 NormalY=0 NormalZ=1 AngleXU=0 Radius=7
    g5: Circle CenterX=91 CenterY=67.5 CenterZ=0 NormalX=0 NormalY=0 NormalZ=1 AngleXU=0 Radius=7
    g6: Circle CenterX=91 CenterY=-67.5 CenterZ=0 NormalX=0 NormalY=0 NormalZ=1 AngleXU=0 Radius=7
    g7: Circle CenterX=-91 CenterY=-241 CenterZ=0 NormalX=0 NormalY=0 NormalZ=1 AngleXU=0 Radius=7
    g8: Circle CenterX=91 CenterY=-241 CenterZ=0 NormalX=0 NormalY=0 NormalZ=1 AngleXU=0 Radius=7
  constraints (14):
    c: DistanceY(g-1,g0) = 241
    c: DistanceX(g0,g-1) = 91
    c: Symmetric(g0,g1,g-2)
    c: DistanceY(g-1,g2) = 67.5
    c: DistanceX(g2,g-1) = 91
    c: DistanceX(g-1,g3) = 12.5
    c: PointOnObject(g3,g-1)
    c: Symmetric(g2,g4,g-1)
    c: Symmetric(g2,g5,g-2)
    c: Symmetric(g5,g6,g-1)
    c: Symmetric(g1,g8,g-1)
    c: Symmetric(g0,g7,g-1)
    c: Equal(g0, g1-g8) x8
    c: Diameter(g0) = 14
FEATURE [PartDesign::Hole] Hole008  label="back panel screw pass-throughs"
  BaseFeature = -> Pocket004
  BaseProfileType = 7
  CustomThreadClearance = 0
  Depth = 5
  DepthType = 0
  Diameter = 4.5
  DrillForDepth = false
  DrillPoint = 1
  DrillPointAngle = 118
  HoleCutCountersinkAngle = 90
  HoleCutCustomValues = false
  HoleCutDepth = 4.5
  HoleCutDiameter = 9
  HoleCutType = 2
  ModelThread = false
  Profile = -> Sketch032
  Suppressed = false
  Tapered = false
  TaperedAngle = 90
  ThreadClass = 0
  ThreadDepth = 5
  ThreadDepthType = 0
  ThreadDiameter = 4
  ThreadDirection = 0
  ThreadFit = 0
  ThreadSize = 11
  ThreadType = 1
  Threaded = false
  UseCustomThreadClearance = false
  expr: Depth = <<dim>>.back_thickness
FEATURE [PartDesign::Body] Body002  label="back panel"
  AllowCompound = false
  Group = -> [Sketch010,Pad004,Sketch032,Sketch024,Pocket004,Hole008]
  Origin = -> Origin004
  Tip = -> Hole008
FEATURE [PartDesign::Fillet] Fillet006  label="Interior fillets"
  Base = -> Thickness001 [Edge18,Edge24,Edge22,Edge20]
  BaseFeature = -> Thickness001
  Radius = 5
  SupportTransform = false
  Suppressed = false
  UseAllEdges = false
  expr: Radius = <<dim>>.front_roundover - <<dim>>.wall_thickness
FEATURE [PartDesign::Pad] Pad017  label="screw posts pad"
  BaseFeature = -> Fillet006
  Direction = (0,0,-1)
  Length = 37.3
  Length2 = 10
  Profile = -> Sketch018
  ReferenceAxis = -> Sketch018 [N_Axis]
  Reversed = true
  SideType = 0
  Suppressed = false
  Type = 0
  Type2 = 0
  expr: Length = <<dim>>.total_depth - <<dim>>.rim_depth - <<dim>>.wall_thickness
FEATURE [PartDesign::Pocket] Pocket003  label="rim pocket"
  BaseFeature = -> Pad017
  Direction = (0,0,1)
  Length = 5.7
  Length2 = 5
  Profile = -> Sketch021
  ReferenceAxis = -> Sketch021 [N_Axis]
  SideType = 0
  Suppressed = false
  Type = 0
  Type2 = 0
  expr: Length = <<dim>>.rim_depth
FEATURE [PartDesign::Pad] Pad015  label="internal baffle pad"
  BaseFeature = -> Pocket003
  Direction = (0,0,-1)
  Length = 37.3
  Length2 = 10
  Profile = -> Sketch031
  ReferenceAxis = -> Sketch031 [N_Axis]
  SideType = 0
  Suppressed = false
  Type = 0
  Type2 = 0
  expr: Length = <<dim>>.total_depth - <<dim>>.rim_depth - <<dim>>.front_thickness
FEATURE [PartDesign::Pad] Pad002  label="bmr support pad"
  BaseFeature = -> Pad015
  Direction = (0,0,-1)
  Length = 4
  Length2 = 10
  Profile = -> Sketch008
  ReferenceAxis = -> Sketch008 [N_Axis]
  SideType = 0
  Suppressed = false
  Type = 0
  Type2 = 0
FEATURE [TechDraw::DrawSVGTemplate] Template
  Height = 210
  Orientation = 1
  Template = /Applications/FreeCAD.app/Contents/Resources/share/Mod/TechDraw/Templates/Default_Template_A4_Landscape.svg
  Width = 297
FEATURE [TechDraw::DrawProjGroupItem] View  label="Front"
  CoarseView = false
  Direction = (0,0,-1)
  Focus = 100
  HardHidden = false
  IsoCount = 0
  IsoHidden = false
  IsoVisible = false
  LockPosition = true
  Perspective = false
  Rotation = 0
  RotationVector = (1,0,0)
  Scale = 0.375
  ScaleType = 2
  ScrubCount = 1
  SeamHidden = false
  SeamVisible = false
  SmoothHidden = false
  SmoothVisible = true
  Source = -> [Hole008]
  Type = 0
  X = 0
  XDirection = (1e-16,1,0)
  Y = 0
FEATURE [TechDraw::DrawProjGroupItem] ProjItem  label="Bottom"
  CoarseView = false
  Direction = (-1,1e-16,0)
  Focus = 100
  HardHidden = false
  IsoCount = 0
  IsoHidden = false
  IsoVisible = false
  LockPosition = false
  Perspective = false
  Rotation = 0
  RotationVector = (1,0,0)
  Scale = 0.375
  ScaleType = 2
  ScrubCount = 1
  SeamHidden = false
  SeamVisible = false
  SmoothHidden = false
  SmoothVisible = true
  Source = -> [Hole008]
  Type = 5
  X = 0
  XDirection = (1e-16,1,0)
  Y = 52.3125
FEATURE [TechDraw::DrawProjGroup] ProjGroup
  Anchor = -> View
  AutoDistribute = true
  LockPosition = false
  ProjectionType = 0
  Rotation = 0
  Scale = 0.375
  ScaleType = 1
  Source = -> [Hole008]
  Views = -> [View,ProjItem]
  X = 150.061
  Y = 129.09
  spacingX = 15
  spacingY = 15
FEATURE [TechDraw::DrawViewDimExtent] DimExtent
  AngleOverride = false
  Arbitrary = false
  ArbitraryTolerances = false
  DirExtent = 0
  EqualTolerance = true
  ExtensionAngle = 0
  FormatSpec = %.2w
  FormatSpecOverTolerance = %+.2w
  FormatSpecUnderTolerance = %+.2w
  Inverted = false
  LineAngle = 0
  LockPosition = false
  MeasureType = 1
  OverTolerance = 0
  References2D = -> [View]
  Rotation = 0
  ScaleType = 0
  ShowUnits = false
  Source = -> [View]
  TheoreticalExact = false
  Type = 1
  UnderTolerance = 0
  UseActualArea = true
  X = 4.31269
  Y = -39.2603
FEATURE [TechDraw::DrawViewDimExtent] DimExtent001
  AngleOverride = false
  Arbitrary = false
  ArbitraryTolerances = false
  DirExtent = 1
  EqualTolerance = true
  ExtensionAngle = 0
  FormatSpec = %.2w
  FormatSpecOverTolerance = %+.2w
  FormatSpecUnderTolerance = %+.2w
  Inverted = false
  LineAngle = 0
  LockPosition = false
  MeasureType = 1
  OverTolerance = 0
  References2D = -> [View]
  Rotation = 0
  ScaleType = 0
  ShowUnits = false
  Source = -> [View]
  TheoreticalExact = false
  Type = 2
  UnderTolerance = 0
  UseActualArea = true
  X = 97.2585
  Y = -5.20496
FEATURE [TechDraw::DrawViewDimExtent] DimExtent002
  AngleOverride = false
  Arbitrary = false
  ArbitraryTolerances = false
  DirExtent = 1
  EqualTolerance = true
  ExtensionAngle = 0
  FormatSpec = %.2w
  FormatSpecOverTolerance = %+.2w
  FormatSpecUnderTolerance = %+.2w
  Inverted = false
  LineAngle = 0
  LockPosition = false
  MeasureType = 1
  OverTolerance = 0
  References2D = -> [ProjItem]
  Rotation = 0
  ScaleType = 0
  ShowUnits = false
  Source = -> [ProjItem]
  TheoreticalExact = false
  Type = 2
  UnderTolerance = 0
  UseActualArea = true
  X = 95.9201
  Y = -4.90754
FEATURE [TechDraw::DrawViewAnnotation] Annotation
  Font = osifont
  LineSpace = 100
  LockPosition = false
  MaxWidth = -1
  Rotation = 0
  ScaleType = 0
  Text = Corner | radius | 7mm
  TextSize = 3
  TextStyle = 0
  X = 48.3271
  Y = 98.1589
FEATURE [TechDraw::DrawViewImage] ActiveView
  Height = 102.4
  ImageFile = <userpath>/Library/Caches/FreeCAD/Cache/FreeCAD_Doc_b72852a3-4320-47ef-8016-d30b04bf8afa_456ddf_487194/PageActiveViewcDX8Vj.png
  LockPosition = false
  Rotation = 0
  ScaleType = 2
  Width = 128
  X = 98.6422
  Y = 59.5398
FEATURE [TechDraw::DrawSVGTemplate] Template001
  Height = 210
  Orientation = 1
  Template = /Applications/FreeCAD.app/Contents/Resources/share/Mod/TechDraw/Templates/Default_Template_A4_Landscape.svg
  Width = 297
FEATURE [TechDraw::DrawViewImage] Image
  Height = 100
  ImageFile = <userpath>/Downloads/Screenshot 2025-10-16 at 9.21.55 am.png
  LockPosition = false
  Rotation = 0
  Scale = 0.75
  ScaleType = 2
  Width = 100
  X = 147.629
  Y = 117.886
FEATURE [TechDraw::DrawViewAnnotation] Annotation003
  Font = osifont
  LineSpace = 100
  LockPosition = false
  MaxWidth = -1
  Owner = -> Image
  Rotation = 0
  ScaleType = 0
  Text = Back panel holes and main body screw post layout
  TextSize = 5
  TextStyle = 0
  X = 0
  Y = 71.7413
FEATURE [TechDraw::DrawPage] Page001  label="Screw holes and posts"
  KeepUpdated = true
  NextBalloonIndex = 1
  ProjectionType = 0
  Template = -> Template001
  Views = -> [Image,Annotation003]
FEATURE [TechDraw::DrawSVGTemplate] Template002
  Height = 210
  Orientation = 1
  Template = /Applications/FreeCAD.app/Contents/Resources/share/Mod/TechDraw/Templates/Default_Template_A4_Landscape.svg
  Width = 297
FEATURE [PartDesign::Chamfer] Chamfer  label="bmr interior chamfer"
  Angle = 45
  Base = -> Pad002 [Edge233]
  BaseFeature = -> Pad002
  ChamferType = 0
  FlipDirection = false
  Size = 2
  Size2 = 1
  SupportTransform = false
  Suppressed = false
  UseAllEdges = false
FEATURE [PartDesign::Pad] Pad001  label="woofer support pad"
  BaseFeature = -> Chamfer
  Direction = (0,0,-1)
  Length = 7
  Length2 = 10
  Profile = -> Sketch003
  ReferenceAxis = -> Sketch003 [N_Axis]
  SideType = 0
  Suppressed = false
  Type = 0
  Type2 = 0
  expr: Length = <<dim>>.woofer_support_thickness
FEATURE [PartDesign::Pocket] Pocket  label="driver holes pocket"
  BaseFeature = -> Pad001
  Direction = (0,0,-1)
  Length = 5
  Length2 = 5
  Profile = -> Sketch001
  ReferenceAxis = -> Sketch001 [N_Axis]
  SideType = 0
  Suppressed = false
  Type = 1
  Type2 = 0
  expr: Length = <<dim>>.wall_thickness
FEATURE [PartDesign::Pocket] Pocket001  label="woofer rebate pocket"
  BaseFeature = -> Pocket
  Direction = (0,0,-1)
  Length = 8
  Length2 = 5
  Profile = -> Sketch002
  ReferenceAxis = -> Sketch002 [N_Axis]
  SideType = 0
  Suppressed = false
  Type = 0
  Type2 = 0
  expr: Length = <<dim>>.woofer_rebate_depth
FEATURE [PartDesign::Pocket] Pocket002  label="bmr rebate pocket"
  BaseFeature = -> Pocket001
  Direction = (0,0,-1)
  Length = 6
  Length2 = 5
  Profile = -> Sketch004
  ReferenceAxis = -> Sketch004 [N_Axis]
  SideType = 0
  Suppressed = false
  Type = 0
  Type2 = 0
  expr: Length = <<dim>>.bmr_rebate_depth
FEATURE [Sketcher::SketchObject] Sketch005  label="bmr screw positions"
  ArcFitTolerance = 1e-06
  AttachmentOffset = pos=(-45,0,0) rot=(0,0,1;0rad)
  AttachmentSupport = -> [Pocket002]
  ExternalTypes = [0]
  FullyConstrained = true
  MakeInternals = false
  MapMode = 5
  Placement = pos=(-45,0,42) rot=(0,0,1;0rad)
  expr: .AttachmentOffset.Base.x = -<<dim>>.bmr_x
  expr: .AttachmentOffset.Base.y = <<dim>>.bmr_y
  expr: Constraints[7] = <<dim>>.bmr_screw_offset
  expr: Constraints[8] = <<dim>>.bmr_screw_offset
  sketch-geometry (4):
    g0: Circle CenterX=16.95 CenterY=-16.95 CenterZ=0 NormalX=0 NormalY=0 NormalZ=1 AngleXU=0 Radius=1.6
    g1: Circle CenterX=16.95 CenterY=16.95 CenterZ=0 NormalX=0 NormalY=0 NormalZ=1 AngleXU=0 Radius=1.6
    g2: Circle CenterX=-16.95 CenterY=16.95 CenterZ=0 NormalX=0 NormalY=0 NormalZ=1 AngleXU=0 Radius=1.6
    g3: Circle CenterX=-16.95 CenterY=-16.95 CenterZ=0 NormalX=0 NormalY=0 NormalZ=1 AngleXU=0 Radius=1.6
  constraints (9):
    c: Equal(g0,g1)
    c: Equal(g0,g2)
    c: Equal(g0,g3)
    c: Diameter(g0) = 3.2
    c: Symmetric(g2,g1,g-2)
    c: Symmetric(g3,g0,g-2)
    c: Symmetric(g2,g3,g-1)
    c: DistanceX(g-1,g1) = 16.95
    c: DistanceY(g-1,g1) = 16.95
FEATURE [Sketcher::SketchObject] Sketch006  label="top woofer screw positions"
  ArcFitTolerance = 1e-06
  AttachmentOffset = pos=(0,120,0) rot=(0,0,1;0rad)
  AttachmentSupport = -> [Pocket001]
  ExternalTypes = [0]
  FullyConstrained = true
  MakeInternals = false
  MapMode = 5
  Placement = pos=(0,120,40) rot=(0,0,1;0rad)
  expr: .AttachmentOffset.Base.x = -<<dim>>.woofer_x
  expr: .AttachmentOffset.Base.y = <<dim>>.woofer_y
  expr: Constraints[7] = <<dim>>.woofer_screw_offset
  expr: Constraints[8] = <<dim>>.woofer_screw_offset
  sketch-geometry (4):
    g0: Circle CenterX=49.5253 CenterY=-49.5253 CenterZ=0 NormalX=0 NormalY=0 NormalZ=1 AngleXU=0 Radius=2
    g1: Circle CenterX=49.5253 CenterY=49.5253 CenterZ=0 NormalX=0 NormalY=0 NormalZ=1 AngleXU=0 Radius=2
    g2: Circle CenterX=-49.5253 CenterY=49.5253 CenterZ=0 NormalX=0 NormalY=0 NormalZ=1 AngleXU=0 Radius=2
    g3: Circle CenterX=-49.5253 CenterY=-49.5253 CenterZ=0 NormalX=0 NormalY=0 NormalZ=1 AngleXU=0 Radius=2
  constraints (9):
    c: Equal(g0,g1)
    c: Equal(g0,g2)
    c: Equal(g0,g3)
    c: Diameter(g0) = 4
    c: Symmetric(g2,g1,g-2)
    c: Symmetric(g3,g0,g-2)
    c: Symmetric(g2,g3,g-1)
    c: DistanceX(g-1,g1) = 49.5253
    c: DistanceY(g-1,g1) = 49.5253
FEATURE [Sketcher::SketchObject] Sketch007  label="bottom woofer screw positions"
  ArcFitTolerance = 1e-06
  AttachmentOffset = pos=(0,-120,0) rot=(0,0,1;0rad)
  AttachmentSupport = -> [Pocket001]
  ExternalTypes = [0]
  FullyConstrained = true
  MakeInternals = true
  MapMode = 5
  Placement = pos=(0,-120,40) rot=(0,0,1;0rad)
  expr: .AttachmentOffset.Base.x = -<<dim>>.woofer_x
  expr: .AttachmentOffset.Base.y = -<<dim>>.woofer_y
  expr: Constraints[7] = <<dim>>.woofer_screw_offset
  expr: Constraints[8] = <<dim>>.woofer_screw_offset
  sketch-geometry (4):
    g0: Circle CenterX=49.5253 CenterY=-49.5253 CenterZ=0 NormalX=0 NormalY=0 NormalZ=1 AngleXU=0 Radius=2
    g1: Circle CenterX=49.5253 CenterY=49.5253 CenterZ=0 NormalX=0 NormalY=0 NormalZ=1 AngleXU=0 Radius=2
    g2: Circle CenterX=-49.5253 CenterY=49.5253 CenterZ=0 NormalX=0 NormalY=0 NormalZ=1 AngleXU=0 Radius=2
    g3: Circle CenterX=-49.5253 CenterY=-49.5253 CenterZ=0 NormalX=0 NormalY=0 NormalZ=1 AngleXU=0 Radius=2
  constraints (9):
    c: Equal(g0,g1)
    c: Equal(g0,g2)
    c: Equal(g0,g3)
    c: Diameter(g0) = 4
    c: Symmetric(g2,g1,g-2)
    c: Symmetric(g3,g0,g-2)
    c: Symmetric(g2,g3,g-1)
    c: DistanceX(g-1,g1) = 49.5253
    c: DistanceY(g-1,g1) = 49.5253
FEATURE [TechDraw::DrawViewImage] ActiveView001
  Height = 102.4
  ImageFile = <userpath>/Library/Caches/FreeCAD/Cache/FreeCAD_Doc_b72852a3-4320-47ef-8016-d30b04bf8afa_456ddf_487194/Page002ActiveView001gEmG7B.png
  LockPosition = false
  Rotation = 0
  ScaleType = 2
  Width = 128
  X = 79.3706
  Y = 107.09
FEATURE [TechDraw::DrawViewImage] Image001
  Height = 100
  ImageFile = <userpath>/Downloads/Screenshot 2025-10-16 at 9.36.40 am.png
  LockPosition = false
  Rotation = 0
  ScaleType = 2
  Width = 100
  X = 189.42
  Y = 107.09
FEATURE [TechDraw::DrawViewAnnotation] Annotation004
  Font = osifont
  LineSpace = 100
  LockPosition = false
  MaxWidth = -1
  Owner = -> Image001
  Rotation = 0
  ScaleType = 0
  Text = Interior baffle detail
  TextSize = 5
  TextStyle = 0
  X = -44.403
  Y = 85.4975
FEATURE [TechDraw::DrawPage] Page002  label="Interior baffle detail"
  KeepUpdated = true
  NextBalloonIndex = 1
  ProjectionType = 0
  Template = -> Template002
  Views = -> [ActiveView001,Image001,Annotation004]
FEATURE [TechDraw::DrawViewAnnotation] Annotation005
  Font = osifont
  LineSpace = 100
  LockPosition = false
  MaxWidth = -1
  Rotation = 0
  ScaleType = 0
  Text = Back panel dimensions
  TextSize = 5
  TextStyle = 0
  X = 150.061
  Y = 195.264
FEATURE [TechDraw::DrawPage] Page  label="Back panel"
  KeepUpdated = true
  NextBalloonIndex = 1
  ProjectionType = 0
  Template = -> Template
  Views = -> [ProjGroup,DimExtent,DimExtent001,DimExtent002,Annotation,ActiveView,Annotation005]
FEATURE [TechDraw::DrawSVGTemplate] Template003
  Height = 210
  Orientation = 1
  Template = /Applications/FreeCAD.app/Contents/Resources/share/Mod/TechDraw/Templates/Default_Template_A4_Landscape.svg
  Width = 297
FEATURE [TechDraw::DrawViewAnnotation] Annotation006
  Font = osifont
  LineSpace = 100
  LockPosition = false
  MaxWidth = -1
  Rotation = 0
  ScaleType = 0
  Text = Sections through driver cutouts
  TextSize = 5
  TextStyle = 0
  X = 139.794
  Y = 200.103
FEATURE [TechDraw::DrawPage] Page003  label="Driver cutout sections"
  KeepUpdated = false
  NextBalloonIndex = 1
  ProjectionType = 0
  Template = -> Template003
  Views = -> [Annotation006]
FEATURE [TechDraw::DrawSVGTemplate] Template004
  Height = 210
  Orientation = 1
  Template = /Applications/FreeCAD.app/Contents/Resources/share/Mod/TechDraw/Templates/Default_Template_A4_Landscape.svg
  Width = 297
FEATURE [TechDraw::DrawViewImage] Image002
  Height = 100
  ImageFile = <userpath>/Downloads/Screenshot 2025-10-16 at 10.15.59 am.png
  LockPosition = false
  Rotation = 0
  Scale = 0.3
  ScaleType = 2
  Width = 100
  X = 59.6084
  Y = 146.498
FEATURE [TechDraw::DrawViewImage] Image003
  Height = 100
  ImageFile = <userpath>/Downloads/Screenshot 2025-10-16 at 10.15.02 am.png
  LockPosition = false
  Rotation = 0
  ScaleType = 2
  Width = 100
  X = 139.377
  Y = 80.7295
FEATURE [TechDraw::DrawViewAnnotation] Annotation007
  Font = osifont
  LineSpace = 100
  LockPosition = false
  MaxWidth = -1
  Owner = -> Image002
  Rotation = 0
  ScaleType = 0
  Text = Driver layout
  TextSize = 5
  TextStyle = 0
  X = 79.7687
  Y = 47.5082
FEATURE [TechDraw::DrawPage] Page004  label="Driver layout"
  KeepUpdated = true
  NextBalloonIndex = 1
  ProjectionType = 0
  Template = -> Template004
  Views = -> [Image002,Image003,Annotation007]
FEATURE [App::DocumentObjectGroup] Group001  label="Drawings"
  Group = -> [Page,Page001,Page002,Page003,Page004]
FEATURE [PartDesign::Chamfer] Chamfer003  label="Front driver hole chamfers"
  Angle = 45
  Base = -> Pocket002 [Edge59,Edge37,Edge58]
  BaseFeature = -> Pocket002
  ChamferType = 0
  FlipDirection = false
  Size = 1.5
  Size2 = 1
  SupportTransform = false
  Suppressed = false
  UseAllEdges = false
FEATURE [PartDesign::Hole] Hole  label="bmr screw holes"
  BaseFeature = -> Chamfer003
  BaseProfileType = 6
  CustomThreadClearance = 0
  Depth = 25
  DepthType = 0
  Diameter = 2.52
  DrillForDepth = false
  DrillPoint = 1
  DrillPointAngle = 118
  HoleCutCountersinkAngle = 90
  HoleCutCustomValues = false
  HoleCutDepth = 0
  HoleCutDiameter = 6.1
  HoleCutType = 0
  ModelThread = true
  Profile = -> Sketch005
  Suppressed = false
  Tapered = false
  TaperedAngle = 90
  ThreadClass = 0
  ThreadDepth = 25
  ThreadDepthType = 0
  ThreadDiameter = 3
  ThreadDirection = 0
  ThreadFit = 0
  ThreadSize = 9
  ThreadType = 1
  Threaded = true
  UseCustomThreadClearance = false
FEATURE [PartDesign::Hole] Hole001  label="top woofer screw holes"
  BaseFeature = -> Hole
  BaseProfileType = 6
  CustomThreadClearance = 0
  Depth = 25
  DepthType = 0
  Diameter = 3.322
  DrillForDepth = false
  DrillPoint = 1
  DrillPointAngle = 118
  HoleCutCountersinkAngle = 90
  HoleCutCustomValues = false
  HoleCutDepth = 0
  HoleCutDiameter = 6.1
  HoleCutType = 0
  ModelThread = true
  Profile = -> Sketch006
  Suppressed = false
  Tapered = false
  TaperedAngle = 90
  ThreadClass = 0
  ThreadDepth = 10
  ThreadDepthType = 1
  ThreadDiameter = 4
  ThreadDirection = 0
  ThreadFit = 0
  ThreadSize = 11
  ThreadType = 1
  Threaded = true
  UseCustomThreadClearance = false
FEATURE [PartDesign::Hole] Hole002  label="bottom woofer screw holes"
  BaseFeature = -> Hole001
  BaseProfileType = 6
  CustomThreadClearance = 0
  Depth = 25
  DepthType = 0
  Diameter = 3.322
  DrillForDepth = false
  DrillPoint = 1
  DrillPointAngle = 118
  HoleCutCountersinkAngle = 90
  HoleCutCustomValues = false
  HoleCutDepth = 0
  HoleCutDiameter = 6.1
  HoleCutType = 0
  ModelThread = true
  Profile = -> Sketch007
  Suppressed = false
  Tapered = false
  TaperedAngle = 90
  ThreadClass = 0
  ThreadDepth = 25
  ThreadDepthType = 0
  ThreadDiameter = 4
  ThreadDirection = 0
  ThreadFit = 0
  ThreadSize = 11
  ThreadType = 1
  Threaded = true
  UseCustomThreadClearance = false
FEATURE [PartDesign::Hole] Hole007  label="back panel post screw holes"
  BaseFeature = -> Hole002
  BaseProfileType = 7
  CustomThreadClearance = 0
  Depth = 20
  DepthType = 0
  Diameter = 3.322
  DrillForDepth = false
  DrillPoint = 1
  DrillPointAngle = 118
  HoleCutCountersinkAngle = 90
  HoleCutCustomValues = false
  HoleCutDepth = 0
  HoleCutDiameter = 0
  HoleCutType = 0
  ModelThread = true
  Profile = -> Sketch018
  Suppressed = false
  Tapered = false
  TaperedAngle = 90
  ThreadClass = 0
  ThreadDepth = 20
  ThreadDepthType = 0
  ThreadDiameter = 4
  ThreadDirection = 0
  ThreadFit = 0
  ThreadSize = 11
  ThreadType = 1
  Threaded = true
  UseCustomThreadClearance = false
FEATURE [PartDesign::Fillet] Fillet  label="Exterior roundovers"
  Base = -> Hole007 [Edge30,Edge31,Edge28,Edge29,Edge80,Edge82,Edge77,Edge78]
  BaseFeature = -> Hole007
  Radius = 10
  SupportTransform = false
  Suppressed = false
  UseAllEdges = false
FEATURE [PartDesign::Body] Body  label="main shell"
  AllowCompound = false
  Group = -> [Sketch,Pad,Thickness001,Fillet006,Pad017,Pocket003,Pad015,Pad002,Chamfer,Pad001,Pocket,Sketch001,Sketch002,Pocket001,Sketch003,Sketch004,Pocket002,Chamfer003,Sketch005,Hole,Sketch006,Hole001,Sketch007,Hole002,Sketch008,Sketch018,Sketch021,Sketch031,Hole007,Fillet]
  Origin = -> Origin
  Tip = -> Fillet
FEATURE [App::Point] Origin021
  Role = Origin
FEATURE [Sketcher::SketchObject] Sketch033
  ArcFitTolerance = 1e-06
  AttachmentOffset = pos=(0,0,5.8) rot=(0,0,1;0rad)
  AttachmentSupport = -> [Origin020]
  ExternalTypes = [0]
  FullyConstrained = true
  MakeInternals = false
  MapMode = 5
  Placement = pos=(0,0,5.8) rot=(0,0,1;0rad)
  sketch-geometry (16):
    g0: LineSegment StartX=-22.5 StartY=-92.5 StartZ=0 EndX=-22.5 EndY=-157.5 EndZ=0
    g1: LineSegment StartX=-22.5 StartY=-157.5 StartZ=0 EndX=22.5 EndY=-157.5 EndZ=0
    g2: LineSegment StartX=22.5 StartY=-157.5 StartZ=0 EndX=22.5 EndY=-92.5 EndZ=0
    g3: LineSegment StartX=22.5 StartY=-92.5 StartZ=0 EndX=-22.5 EndY=-92.5 EndZ=0
    g4: LineSegment StartX=-72.5 StartY=32.5 StartZ=0 EndX=-72.5 EndY=-32.5 EndZ=0
    g5: LineSegment StartX=-72.5 StartY=-32.5 StartZ=0 EndX=-27.5 EndY=-32.5 EndZ=0
    g6: LineSegment StartX=-27.5 StartY=-32.5 StartZ=0 EndX=-27.5 EndY=32.5 EndZ=0
    g7: LineSegment StartX=-27.5 StartY=32.5 StartZ=0 EndX=-72.5 EndY=32.5 EndZ=0
    g8: LineSegment StartX=27.5 StartY=32.5 StartZ=0 EndX=27.5 EndY=-32.5 EndZ=0
    g9: LineSegment StartX=27.5 StartY=-32.5 StartZ=0 EndX=72.5 EndY=-32.5 EndZ=0
    g10: LineSegment StartX=72.5 StartY=-32.5 StartZ=0 EndX=72.5 EndY=32.5 EndZ=0
    g11: LineSegment StartX=72.5 StartY=32.5 StartZ=0 EndX=27.5 EndY=32.5 EndZ=0
    g12: LineSegment StartX=-22.5 StartY=157.5 StartZ=0 EndX=-22.5 EndY=92.5 EndZ=0
    g13: LineSegment StartX=-22.5 StartY=92.5 StartZ=0 EndX=22.5 EndY=92.5 EndZ=0
    g14: LineSegment StartX=22.5 StartY=92.5 StartZ=0 EndX=22.5 EndY=157.5 EndZ=0
    g15: LineSegment StartX=22.5 StartY=157.5 StartZ=0 EndX=-22.5 EndY=157.5 EndZ=0
  constraints (42):
    c: Coincident(g0,g1)
    c: Coincident(g1,g2)
    c: Coincident(g2,g3)
    c: Coincident(g3,g0)
    c: Vertical(g0)
    c: Vertical(g2)
    c: Horizontal(g1)
    c: DistanceX(g3,g3) = 45
    c: DistanceY(g0,g0) = 65
    c: Coincident(g4,g5)
    c: Coincident(g5,g6)
    c: Coincident(g6,g7)
    c: Coincident(g7,g4)
    c: Vertical(g4)
    c: Horizontal(g5)
    c: Horizontal(g7)
    c: DistanceX(g7,g7) = 45
    c: DistanceY(g4,g4) = 65
    c: Coincident(g8,g9)
    c: Coincident(g9,g10)
    c: Coincident(g10,g11)
    c: Coincident(g11,g8)
    c: Vertical(g10)
    c: Horizontal(g9)
    c: Horizontal(g11)
    c: DistanceX(g11,g11) = 45
    c: Coincident(g12,g13)
    c: Coincident(g13,g14)
    c: Coincident(g14,g15)
    c: Coincident(g15,g12)
    c: Vertical(g12)
    c: Vertical(g14)
    c: Horizontal(g13)
    c: DistanceY(g12,g12) = 65
    c: Symmetric(g12,g14,g-2)
    c: Symmetric(g6,g5,g-1)
    c: Symmetric(g8,g8,g-1)
    c: Symmetric(g2,g0,g-2)
    c: DistanceX(g6,g8) = 55
    c: Symmetric(g6,g8,g-2)
    c: Symmetric(g13,g2,g-1)
    c: DistanceY(g2,g13) = 185
FEATURE [PartDesign::Pad] Pad018
  Direction = (0,0,1)
  Length = 0.55
  Length2 = 10
  Profile = -> Sketch033
  ReferenceAxis = -> Sketch033 [N_Axis]
  SideType = 0
  Suppressed = false
  Type = 0
  Type2 = 0
FEATURE [PartDesign::Body] Body009  label="CLD tiles"
  AllowCompound = true
  Group = -> [Sketch033,Pad018]
  Origin = -> Origin020
  Tip = -> Pad018
FEATURE [App::Point] Origin023
  Role = Origin
FEATURE [PartDesign::SubShapeBinder] Binder
  BindCopyOnChange = 0
  BindMode = 0
  ClaimChildren = false
  Context = -> Body010 [Binder.]
  Fuse = false
  MakeFace = true
  OffsetFill = false
  OffsetIntersection = false
  OffsetJoinType = 0
  OffsetOpenResult = false
  PartialLoad = false
  Refine = true
  Relative = true
  Support = -> [Body002[Hole008.Face5]]
  _Version = 2
FEATURE [PartDesign::Pad] Pad019
  Direction = (0,0,1)
  Length = 0.8
  Length2 = 10
  Profile = -> Binder
  SideType = 0
  Suppressed = false
  Type = 0
  Type2 = 0
FEATURE [PartDesign::Body] Body010  label="back panel gasket"
  AllowCompound = false
  Group = -> [Binder,Pad019]
  Origin = -> Origin022
  Tip = -> Pad019
FEATURE [App::DocumentObjectGroup] Group002  label="Gaskets"
  Group = -> [Body004,Body007,Body010]
FEATURE [Mesh::Feature] Mesh  label="main shell (Meshed)"
FEATURE [PartDesign::Chamfer] Chamfer004
  Angle = 45
  Base = -> Pad013 [Edge10]
  BaseFeature = -> Pad013
  ChamferType = 1
  FlipDirection = false
  Size = 1.5
  Size2 = 9
  SupportTransform = false
  Suppressed = false
  UseAllEdges = false
FEATURE [PartDesign::Pocket] Pocket005  label="frame pocket"
  BaseFeature = -> Chamfer004
  Direction = (0,0,-1)
  Length = 5
  Length2 = 5
  Profile = -> Sketch015
  ReferenceAxis = -> Sketch015 [N_Axis]
  SideType = 0
  Suppressed = false
  Type = 0
  Type2 = 0
FEATURE [Sketcher::SketchObject] Sketch029
  ArcFitTolerance = 1e-06
  AttachmentSupport = -> [Pocket005]
  ExternalTypes = [0]
  FullyConstrained = true
  MakeInternals = false
  MapMode = 45
  Placement = pos=(-16.7767,16.7756,4.52871) rot=(0.031836,-0.013188,0.999406;2.35661rad)
  sketch-geometry (1):
    g0: Circle CenterX=-16.95 CenterY=16.95 CenterZ=0 NormalX=0 NormalY=0 NormalZ=1 AngleXU=0 Radius=1.6
  constraints (3):
    c: Diameter(g0) = 3.2
    c: DistanceX(g0,g-1) = 16.95
    c: DistanceY(g-1,g0) = 16.95
FEATURE [PartDesign::Pocket] Pocket006
  BaseFeature = -> Pocket005
  Direction = (-0.0450027,0.0450052,-0.997973)
  Length = 5
  Length2 = 5
  Profile = -> Sketch029
  ReferenceAxis = -> Sketch029 [N_Axis]
  SideType = 0
  Suppressed = false
  Type = 0
  Type2 = 0
FEATURE [PartDesign::PolarPattern] PolarPattern
  Angle = 360
  Axis = -> Z_Axis003
  BaseFeature = -> Pocket006
  Mode = 0
  Occurrences = 4
  Offset = 120
  SpacingPattern = [0]
  Spacings = [-1,-1,-1]
  Suppressed = false
  TransformMode = 1
FEATURE [PartDesign::Body] Body003  label="Tweeter ring"
  AllowCompound = false
  Group = -> [Sketch015,Sketch027,Pad013,Sketch029,Chamfer004,Pocket005,Pocket006,PolarPattern]
  Origin = -> Origin006
  Placement = pos=(-45,0,42.7) rot=(0,0,1;0rad)
  Tip = -> PolarPattern
FEATURE [App::DocumentObjectGroup] Group003  label="Separate parts"
  Group = -> [Body003,Body008,Body009]
FEATURE [Part::Feature] Body_cs
  shape: bbox 200 x 0.0005433 x 48 mm, 0 faces, 0 solids (baked)
